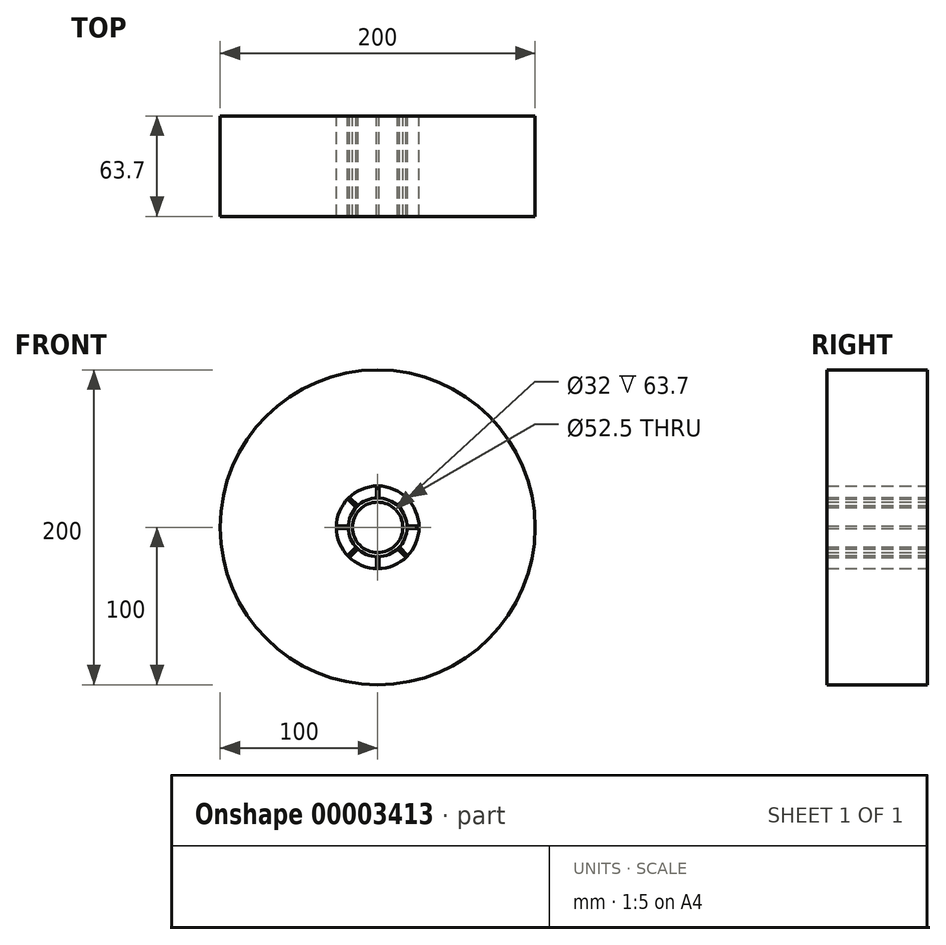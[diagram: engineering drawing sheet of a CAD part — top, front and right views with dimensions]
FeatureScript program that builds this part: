
annotation { "Feature Type Name" : "Feature", "Feature Type Description" : "" }
export const myFeature = defineFeature(function(context is Context, id is Id, definition is map)
    precondition{}
    {
        {
            var Q0;
            Q0=qCreatedBy(makeId("Front.planeOp"),FACE);
            var sketch = newSketch(context, id + "F0", { "sketchPlane" : qUnion([Q0])});
            skCircle(sketch, "E0", {"center": v(0, 0) * mm, "radius": 16 * mm});
            skCircle(sketch, "E1", {"center": v(0, 0) * mm, "radius": 26.25 * mm});
            skCircle(sketch, "E2", {"center": v(0, 0) * mm, "radius": 18.66 * mm});
            skCircle(sketch, "E3", {"center": v(0, 0) * mm, "radius": 100 * mm});
            skLineSegment(sketch, "E4", {"start": v(-0.82, 26.24) * mm, "end": v(-0.81, 18.64) * mm});
            skLineSegment(sketch, "E5", {"start": v(0.82, 18.64) * mm, "end": v(0.82, 26.24) * mm});
            skLineSegment(sketch, "E6", {"start": v(0.82, 26.24) * mm, "end": v(-0.82, 26.24) * mm, "construction": true});
            skPoint(sketch, "E7", {"position": v(0, 26.24) * mm});
            skPoint(sketch, "E8", {"position": v(0.82, 26.24) * mm});
            skPoint(sketch, "E9", {"position": v(-0.82, 26.24) * mm});
            skSolve(sketch);
        }
        {
            var Q0;
            Q0=makeQuery(id+"F0.imprint","IMPRINT",FACE,{"disambiguationData":[TD([[makeQuery(id+"F0.imprint","IMPRINT",EDGE,{"derivedFrom":sQuery(id+"F0.wireOp",EDGE,"E0")}),-1.0]])]});
            var Q1;
            Q1=makeQuery(id+"F0.imprint","IMPRINT",FACE,{"disambiguationData":[TD([[makeQuery(id+"F0.imprint","IMPRINT",EDGE,{"derivedFrom":sQuery(id+"F0.wireOp",EDGE,"E3")}),1.0]])]});
            extrude(context, id + "F1", {"entities" : qUnion([Q0, Q1]), "depth" : 63.7 * mm});
        }
        {
            var Q0;
            {var subQ1=sQuery(id+"F0.wireOp",EDGE,"E4");Q0=makeQuery(id+"F0.imprint","IMPRINT",FACE,{"disambiguationData":[TD([[makeQuery(id+"F0.imprint","IMPRINT",EDGE,{"derivedFrom":subQ1}),1.0]])]});}
            extrude(context, id + "F2", {"entities" : qUnion([Q0]), "depth" : 63.7 * mm});
        }
        {
            var Q0;
            Q0=makeQuery(id+"F2.opExtrude","SWEPT_BODY",BODY,{"disambiguationData":[OSD([sQuery(id+"F0.wireOp",EDGE,"E1"),sQuery(id+"F0.wireOp",EDGE,"E2"),sQuery(id+"F0.wireOp",EDGE,"E4"),sQuery(id+"F0.wireOp",EDGE,"E5")])]});
            var Q1;
            Q1=makeQuery(id+"F1.opExtrude","SWEPT_FACE",FACE,{"disambiguationData":[OSD([sQuery(id+"F0.wireOp",EDGE,"E0")])]});
            circularPattern(context, id + "F3", {"entities" : qUnion([Q0]), "axis" : qUnion([Q1]), "angle" : 45 * degree, "instanceCount" : 8});
        }
    });
